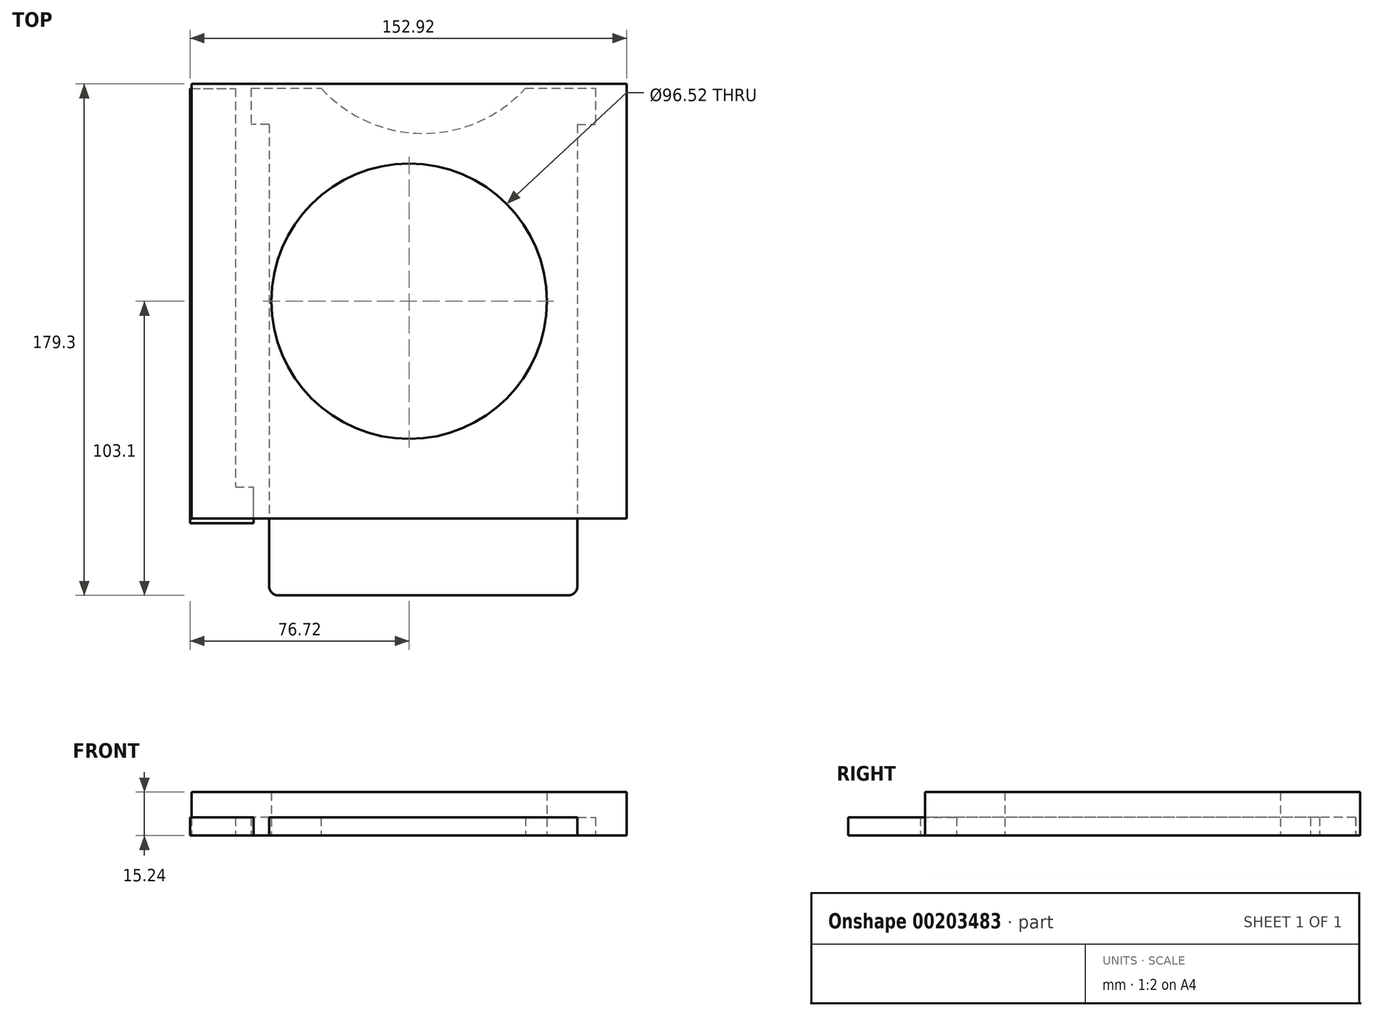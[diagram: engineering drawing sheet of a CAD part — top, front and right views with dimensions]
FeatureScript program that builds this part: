
annotation { "Feature Type Name" : "Feature", "Feature Type Description" : "" }
export const myFeature = defineFeature(function(context is Context, id is Id, definition is map)
    precondition{}
    {
        {
            var Q0;
            Q0=qCreatedBy(makeId("Top.planeOp"),FACE);
            var sketch = newSketch(context, id + "F0", { "sketchPlane" : qUnion([Q0])});
            skLineSegment(sketch, "E0.bottom", {"start": v(76.2, -76.2) * mm, "end": v(-76.2, -76.2) * mm});
            skLineSegment(sketch, "E0.top", {"start": v(76.2, 76.2) * mm, "end": v(-76.2, 76.2) * mm});
            skLineSegment(sketch, "E0.left", {"start": v(76.2, -76.2) * mm, "end": v(76.2, 76.2) * mm});
            skLineSegment(sketch, "E0.right", {"start": v(-76.2, -76.2) * mm, "end": v(-76.2, 76.2) * mm});
            skPoint(sketch, "E0.middle", {"position": v(0, 0) * mm});
            skCircle(sketch, "E1", {"center": v(0, 0) * mm, "radius": 48.26 * mm});
            skSolve(sketch);
        }
        {
            var Q0;
            Q0=qCreatedBy(makeId("Top.planeOp"),FACE);
            var sketch = newSketch(context, id + "F1", { "sketchPlane" : qUnion([Q0])});
            skLineSegment(sketch, "E2.bottom", {"start": v(-49.06, 74.7) * mm, "end": v(-30.85, 74.7) * mm});
            skLineSegment(sketch, "E2.top", {"start": v(-45.88, -103.1) * mm, "end": v(55.72, -103.1) * mm});
            skLineSegment(sketch, "E2.left", {"start": v(-49.06, 62) * mm, "end": v(-49.06, -99.93) * mm});
            skLineSegment(sketch, "E2.right", {"start": v(58.9, 62) * mm, "end": v(58.9, -99.93) * mm});
            skLineSegment(sketch, "E3.bottom", {"start": v(58.9, 74.7) * mm, "end": v(65.24, 74.7) * mm});
            skLineSegment(sketch, "E3.top", {"start": v(58.9, 62) * mm, "end": v(65.24, 62) * mm});
            skLineSegment(sketch, "E3.right", {"start": v(65.24, 74.7) * mm, "end": v(65.24, 62) * mm});
            skLineSegment(sketch, "E4.bottom", {"start": v(-49.06, 74.7) * mm, "end": v(-55.4, 74.7) * mm});
            skLineSegment(sketch, "E4.top", {"start": v(-49.06, 62) * mm, "end": v(-55.4, 62) * mm});
            skLineSegment(sketch, "E4.right", {"start": v(-55.4, 74.7) * mm, "end": v(-55.4, 62) * mm});
            skArc(sketch, "E5", {"start": v(-30.85, 74.7) * mm, "mid": v(4.92, 58.83) * mm, "end": v(40.7, 74.7) * mm});
            skLineSegment(sketch, "E6.trimOffspring", {"start": v(40.7, 74.7) * mm, "end": v(58.9, 74.7) * mm});
            skPoint(sketch, "E7.visualSharp", {"position": v(58.9, -103.1) * mm});
            skArc(sketch, "E7.filletArc", {"start": v(55.72, -103.1) * mm, "mid": v(57.96, -102.17) * mm, "end": v(58.9, -99.93) * mm});
            skPoint(sketch, "E8.visualSharp", {"position": v(-49.06, -103.1) * mm});
            skArc(sketch, "E8.filletArc", {"start": v(-49.06, -99.93) * mm, "mid": v(-48.13, -102.17) * mm, "end": v(-45.88, -103.1) * mm});
            skSolve(sketch);
        }
        {
            var Q0;
            Q0=qCreatedBy(makeId("Top.planeOp"),FACE);
            var sketch = newSketch(context, id + "F2", { "sketchPlane" : qUnion([Q0])});
            skPoint(sketch, "E9.middle", {"position": v(-0.52, -1.61) * mm});
            skLineSegment(sketch, "E10.bottom", {"start": v(-76.72, 74.59) * mm, "end": v(-60.84, 74.59) * mm});
            skLineSegment(sketch, "E10.top", {"start": v(-76.72, -77.81) * mm, "end": v(-60.84, -77.81) * mm});
            skLineSegment(sketch, "E10.left", {"start": v(-76.72, 74.59) * mm, "end": v(-76.72, -77.81) * mm});
            skLineSegment(sketch, "E10.right", {"start": v(-60.84, 74.59) * mm, "end": v(-60.84, -65.11) * mm});
            skLineSegment(sketch, "E11.bottom", {"start": v(-60.84, -77.81) * mm, "end": v(-54.5, -77.81) * mm});
            skLineSegment(sketch, "E11.top", {"start": v(-60.84, -65.11) * mm, "end": v(-54.5, -65.11) * mm});
            skLineSegment(sketch, "E11.right", {"start": v(-54.5, -77.81) * mm, "end": v(-54.5, -65.11) * mm});
            skSolve(sketch);
        }
        {
            var Q0;
            Q0 = qSketchRegion(id + "F0", true);
            extrude(context, id + "F3", {"entities" : qUnion([Q0]), "depth" : 15.24 * mm});
        }
        {
            var Q0;
            Q0 = qSketchRegion(id + "F1", true);
            extrude(context, id + "F4", {"entities" : qUnion([Q0]), "depth" : 6.35 * mm});
        }
        {
            var Q0;
            Q0 = qSketchRegion(id + "F2", true);
            extrude(context, id + "F5", {"entities" : qUnion([Q0]), "depth" : 6.35 * mm});
        }
    });
